# Revit family: IS_Tipica_T2385_BIM_FR
name_source: partatom
category: Plumbing Fixtures
revit_build: Autodesk Revit 2017 (Build: 20160225_1515(x64)
units: mm (PartAtom-declared; Revit-internal decimal feet)

## family parameters
Always vertical = No
Cut with Voids When Loaded = No
OmniClass Number = 23.45.05.14.21.11
OmniClass Title = Bath/Shower Units
Part Type = Normal
Room Calculation Point = No
Round Connector Dimension = Use Diameter
Shared = No
Work Plane-Based = No

## types (2) — shared parameters
Accessoires = www.idealspec.fr
Auteur = Ideal Standard
BOSUseNativeGeometries = 1
Bim-NomDuProjet = ISI_IdealStandard_ShowerEnclosures_Tipica_T2385
Caractéristiques = TIPICA PV Porte de douche  80 cm verre transparent
CodeBarre = 8014140336099
Conformité = NF
ConseilsDInstallation = 0
Couleur = clair
DateDeCréation = 2018_08_03
Description = TIPICA PV Porte de douche  80 cm verre transparent
Dimensions = 770 x 43 x 1870 mm
EAN code = https://8014140336099
Espace = Interne
Finition = clair
Forme = rectangulaire
Hauteur = 1870 mm  [stored 6.13517 ft]
IfcExportAs = Shower enclosures
IfcExportType = IfcSanitaryTerminalType
InformationsProduit = www.idealspec.fr
Largeur = 43 mm
Longueur = 770 mm
Marque = Ideal Standard
Matériel = Glass
Model = T2385YB
Nom = ShowerEnclosures_Tipica_T2385_IdealStandard
PoidsNet = 15,00 KG
Raccordement = Plomberie
Receveur = No
Révision = 1
URL = www.idealspec.fr
Uniclass2015Code = Pr_40_20_06_79
Uniclass2015Title = Shower enclosures
Uniclass2015Version = Products v1.1
UnitéDeMesure = Millimètres
UnitéDeTemps = An
UnitéMonétaire = €
UrlDuFabricant = www.idealspec.fr
Version = 1
zero-valued in all types: Cost, CoûtDeRemplacement, DiamètreÉvacuation, Profondeur

## type names (no varying parameters)
- T2385YB - TIPICA PV PAROI 80 TSP ARG BR
- T2385AC - TIPICA PORTE PV 80 TRANSP. BLC

note: [stored X ft] marks values corroborated as IEEE doubles in the binary element streams (Revit-internal decimal feet)

## geometry (parser evidence)
native form markers: Sweep x2
no freeform markers — native parametric forms only
